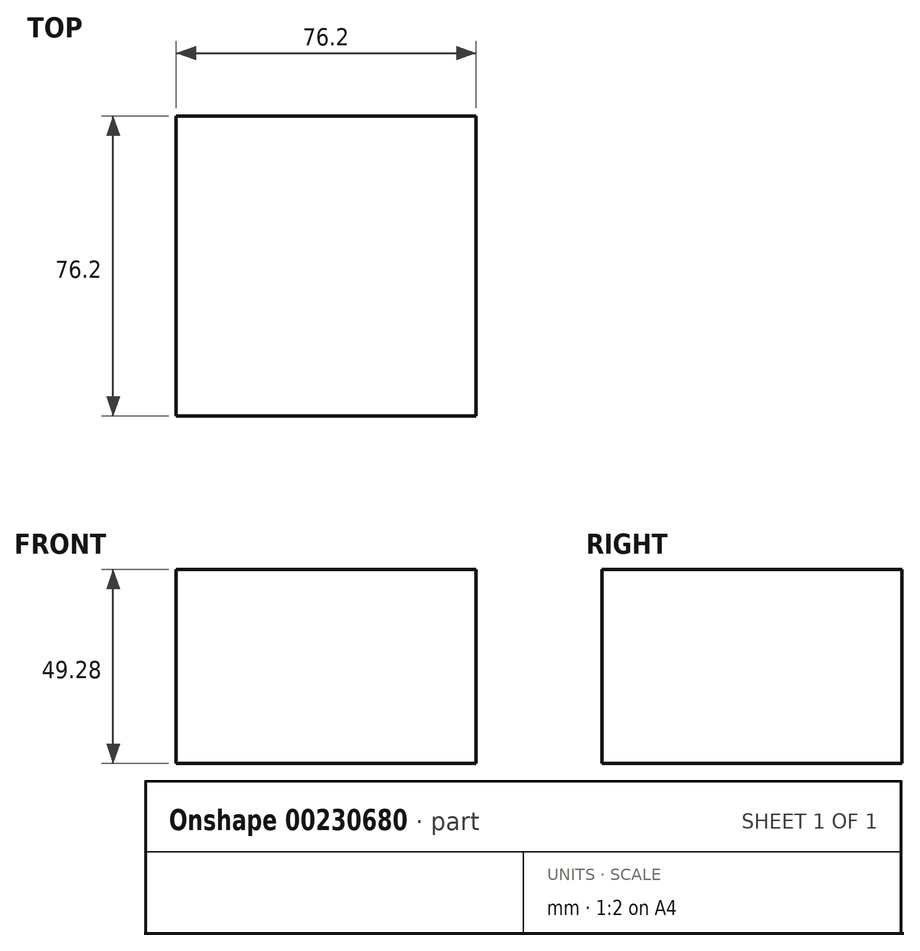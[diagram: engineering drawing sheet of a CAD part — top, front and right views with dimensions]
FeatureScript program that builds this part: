
annotation { "Feature Type Name" : "Feature", "Feature Type Description" : "" }
export const myFeature = defineFeature(function(context is Context, id is Id, definition is map)
    precondition{}
    {
        {
            var Q0;
            Q0=qCreatedBy(makeId("Front.planeOp"),FACE);
            var sketch = newSketch(context, id + "F0", { "sketchPlane" : qUnion([Q0])});
            skLineSegment(sketch, "E0.bottom", {"start": v(38.1, 24.64) * mm, "end": v(-38.1, 24.64) * mm});
            skLineSegment(sketch, "E0.top", {"start": v(38.1, -24.64) * mm, "end": v(-38.1, -24.64) * mm});
            skLineSegment(sketch, "E0.left", {"start": v(38.1, 24.64) * mm, "end": v(38.1, -24.64) * mm});
            skLineSegment(sketch, "E0.right", {"start": v(-38.1, 24.64) * mm, "end": v(-38.1, -24.64) * mm});
            skPoint(sketch, "E0.middle", {"position": v(0, 0) * mm});
            skSolve(sketch);
        }
        {
            var Q0;
            Q0=makeQuery(id+"F0.imprint","IMPRINT",FACE,{"disambiguationData":[TD([[makeQuery(id+"F0.imprint","IMPRINT",EDGE,{"derivedFrom":sQuery(id+"F0.wireOp",EDGE,"E0.bottom")}),1.0]])]});
            extrude(context, id + "F1", {"entities" : qUnion([Q0]), "depth" : 76.2 * mm});
        }
    });
